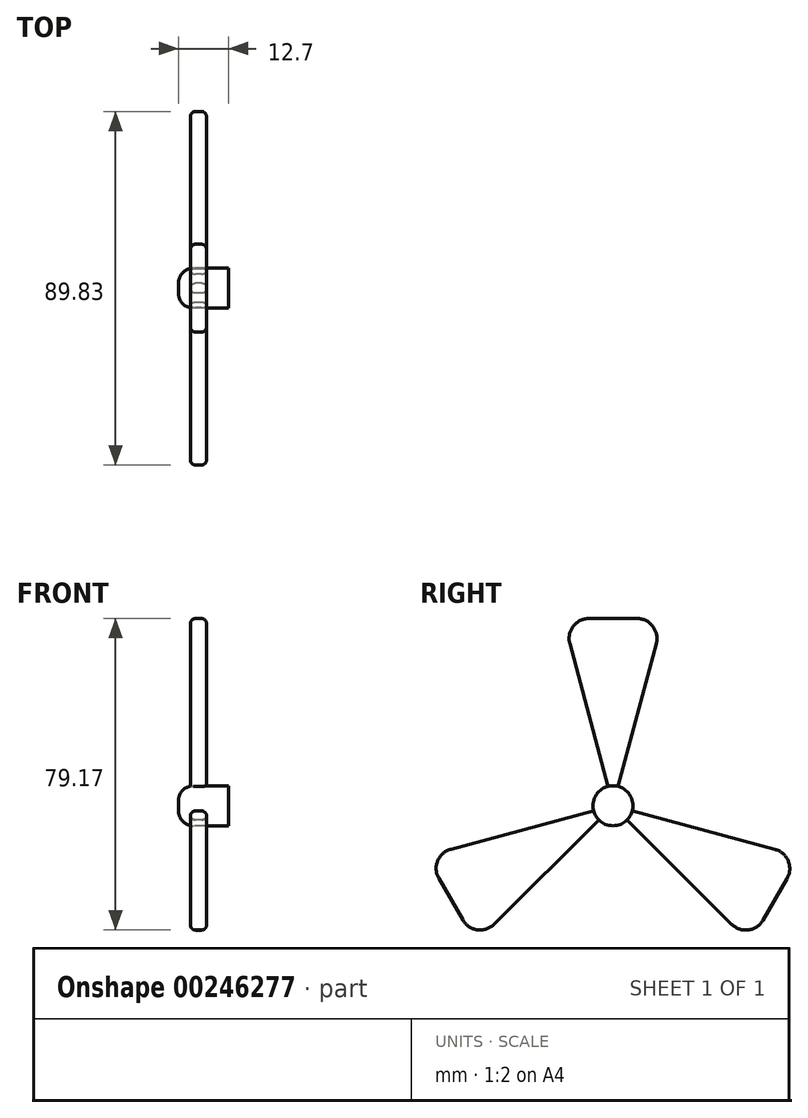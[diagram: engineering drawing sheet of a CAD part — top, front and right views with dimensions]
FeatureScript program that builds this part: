
annotation { "Feature Type Name" : "Feature", "Feature Type Description" : "" }
export const myFeature = defineFeature(function(context is Context, id is Id, definition is map)
    precondition{}
    {
        {
            var Q0;
            Q0=qCreatedBy(makeId("Right.planeOp"),FACE);
            var sketch = newSketch(context, id + "F0", { "sketchPlane" : qUnion([Q0])});
            skLineSegment(sketch, "E0", {"start": v(-6.07, 47.57) * mm, "end": v(6.1, 47.57) * mm});
            skLineSegment(sketch, "E1", {"start": v(-10.98, 41.17) * mm, "end": v(0.01, 0.06) * mm});
            skPoint(sketch, "E1.endSnap0", {"position": v(0.01, 47.57) * mm});
            skLineSegment(sketch, "E2", {"start": v(0.01, 0.06) * mm, "end": v(11, 41.17) * mm});
            skPoint(sketch, "E3.visualSharp", {"position": v(-12.69, 47.57) * mm});
            skArc(sketch, "E3.filletArc", {"start": v(-6.07, 47.57) * mm, "mid": v(-10.1, 45.58) * mm, "end": v(-10.98, 41.17) * mm});
            skPoint(sketch, "E4.visualSharp", {"position": v(12.71, 47.57) * mm});
            skArc(sketch, "E4.filletArc", {"start": v(11, 41.17) * mm, "mid": v(10.13, 45.58) * mm, "end": v(6.1, 47.57) * mm});
            skCircle(sketch, "E5", {"center": v(0, 0) * mm, "radius": 2.54 * mm, "construction": true});
            skPoint(sketch, "E6.1.0", {"position": v(41.19, -23.8) * mm});
            skLineSegment(sketch, "E6.1.1", {"start": v(41.15, -11.08) * mm, "end": v(0.04, -0.04) * mm});
            skPoint(sketch, "E6.1.2", {"position": v(47.54, -12.8) * mm});
            skLineSegment(sketch, "E6.1.3", {"start": v(44.23, -18.53) * mm, "end": v(38.15, -29.06) * mm});
            skPoint(sketch, "E6.1.4", {"position": v(34.84, -34.8) * mm});
            skArc(sketch, "E6.1.5", {"start": v(44.23, -18.53) * mm, "mid": v(44.52, -14.04) * mm, "end": v(41.15, -11.08) * mm});
            skArc(sketch, "E6.1.6", {"start": v(30.16, -30.12) * mm, "mid": v(34.41, -31.56) * mm, "end": v(38.15, -29.06) * mm});
            skLineSegment(sketch, "E6.1.7", {"start": v(0.04, -0.04) * mm, "end": v(30.16, -30.12) * mm});
            skPoint(sketch, "E6.2.0", {"position": v(-41.2, -23.77) * mm});
            skLineSegment(sketch, "E6.2.1", {"start": v(-30.17, -30.1) * mm, "end": v(-0.06, -0.02) * mm});
            skPoint(sketch, "E6.2.2", {"position": v(-34.85, -34.77) * mm});
            skLineSegment(sketch, "E6.2.3", {"start": v(-38.16, -29.04) * mm, "end": v(-44.24, -18.5) * mm});
            skPoint(sketch, "E6.2.4", {"position": v(-47.55, -12.77) * mm});
            skArc(sketch, "E6.2.5", {"start": v(-38.16, -29.04) * mm, "mid": v(-34.42, -31.54) * mm, "end": v(-30.17, -30.1) * mm});
            skArc(sketch, "E6.2.6", {"start": v(-41.16, -11.06) * mm, "mid": v(-44.54, -14.02) * mm, "end": v(-44.24, -18.5) * mm});
            skLineSegment(sketch, "E6.2.7", {"start": v(-0.06, -0.02) * mm, "end": v(-41.16, -11.06) * mm});
            skLineSegment(sketch, "E6.anchor1", {"start": v(0, 0) * mm, "end": v(0.01, 0.06) * mm, "construction": true});
            skLineSegment(sketch, "E6.anchor2", {"start": v(0, 0) * mm, "end": v(-0.06, -0.02) * mm, "construction": true});
            skLineSegment(sketch, "E7", {"start": v(0.04, -0.04) * mm, "end": v(0.01, 47.57) * mm, "construction": true});
            skSolve(sketch);
        }
        {
            var Q0;
            Q0=qCreatedBy(makeId("Front.planeOp"),FACE);
            var sketch = newSketch(context, id + "F1", { "sketchPlane" : qUnion([Q0])});
            skLineSegment(sketch, "E8", {"start": v(-19.02, 0) * mm, "end": v(14.9, 0) * mm, "construction": true});
            skLineSegment(sketch, "E9", {"start": v(0, 5.08) * mm, "end": v(7.62, 5.08) * mm});
            skLineSegment(sketch, "E10", {"start": v(7.62, 5.08) * mm, "end": v(7.62, 0) * mm});
            skLineSegment(sketch, "E11", {"start": v(0, 5.08) * mm, "end": v(-5.08, 5.08) * mm});
            skLineSegment(sketch, "E12", {"start": v(-5.08, 5.08) * mm, "end": v(-5.08, 0) * mm});
            skLineSegment(sketch, "E13", {"start": v(-5.08, 0) * mm, "end": v(7.62, 0) * mm});
            skSolve(sketch);
        }
        {
            var Q0;
            Q0 = qSketchRegion(id + "F1", true);
            var Q1;
            Q1=sQuery(id+"F1.wireOp",EDGE,"E8");
            revolve(context, id + "F2", {"entities" : qUnion([Q0]), "axis" : qUnion([Q1]), "revolveType" : RevolveType.FULL});
        }
        {
            var Q0;
            Q0 = qSketchRegion(id + "F0", true);
            extrude(context, id + "F3", {"entities" : qUnion([Q0]), "operationType" : NewBodyOperationType.ADD, "endBound" : BoundingType.SYMMETRIC, "oppositeDirection" : true, "depth" : 4.06 * mm});
        }
        {
            var Q0;
            Q0=makeQuery(id+"F2.opRevolve","SWEPT_FACE",FACE,{"disambiguationData":[OSD([sQuery(id+"F1.wireOp",EDGE,"E12")])]});
            fillet(context, id + "F4", {"entities" : qUnion([Q0]), "radius" : 3.8 * mm, "tangentPropagation" : true, "allowEdgeOverflow" : false});
        }
        {
            var Q0;
            Q0=makeQuery(id+"F3.opExtrude","CAP_EDGE",EDGE,{"disambiguationData":[OSD([sQuery(id+"F0.wireOp",EDGE,"E6.2.7")])],"isStart":true});
            fillet(context, id + "F5", {"entities" : qUnion([Q0]), "radius" : 1.27 * mm, "tangentPropagation" : true, "allowEdgeOverflow" : false});
        }
        {
            var Q0;
            Q0=makeQuery(id+"F3.opExtrude","CAP_EDGE",EDGE,{"disambiguationData":[OSD([sQuery(id+"F0.wireOp",EDGE,"E6.1.7")])],"isStart":true});
            fillet(context, id + "F6", {"entities" : qUnion([Q0]), "radius" : 1.27 * mm, "tangentPropagation" : true, "allowEdgeOverflow" : false});
        }
        {
            var Q0;
            Q0=makeQuery(id+"F3.opExtrude","CAP_EDGE",EDGE,{"disambiguationData":[OSD([sQuery(id+"F0.wireOp",EDGE,"E1")])],"isStart":true});
            fillet(context, id + "F7", {"entities" : qUnion([Q0]), "radius" : 1.27 * mm, "tangentPropagation" : true, "allowEdgeOverflow" : false});
        }
        {
            var Q0;
            Q0=makeQuery(id+"F3.opExtrude","CAP_EDGE",EDGE,{"disambiguationData":[OSD([sQuery(id+"F0.wireOp",EDGE,"E2")])],"isStart":false});
            var Q1;
            Q1=makeQuery(id+"F3.opExtrude","CAP_EDGE",EDGE,{"disambiguationData":[OSD([sQuery(id+"F0.wireOp",EDGE,"E6.1.1")])],"isStart":false});
            var Q2;
            Q2=makeQuery(id+"F3.opExtrude","CAP_EDGE",EDGE,{"disambiguationData":[OSD([sQuery(id+"F0.wireOp",EDGE,"E6.2.1")])],"isStart":false});
            fillet(context, id + "F8", {"entities" : qUnion([Q0, Q1, Q2]), "radius" : 1.27 * mm, "tangentPropagation" : true, "allowEdgeOverflow" : false});
        }
        {
            var Q0;
            Q0=makeQuery(id+"F2.opRevolve","SWEPT_BODY",BODY,{"disambiguationData":[OSD([sQuery(id+"F1.wireOp",EDGE,"E9"),sQuery(id+"F1.wireOp",EDGE,"E10"),sQuery(id+"F1.wireOp",EDGE,"E11"),sQuery(id+"F1.wireOp",EDGE,"E12"),sQuery(id+"F1.wireOp",EDGE,"E13")])]});
            transform(context, id + "F9", {"entities" : qUnion([Q0]), "transformType" : TransformType.TRANSLATION_3D, "dx" : 0 * mm, "dy" : 0 * mm, "dz" : 0 * mm, "makeCopy" : true});
        }
    });
